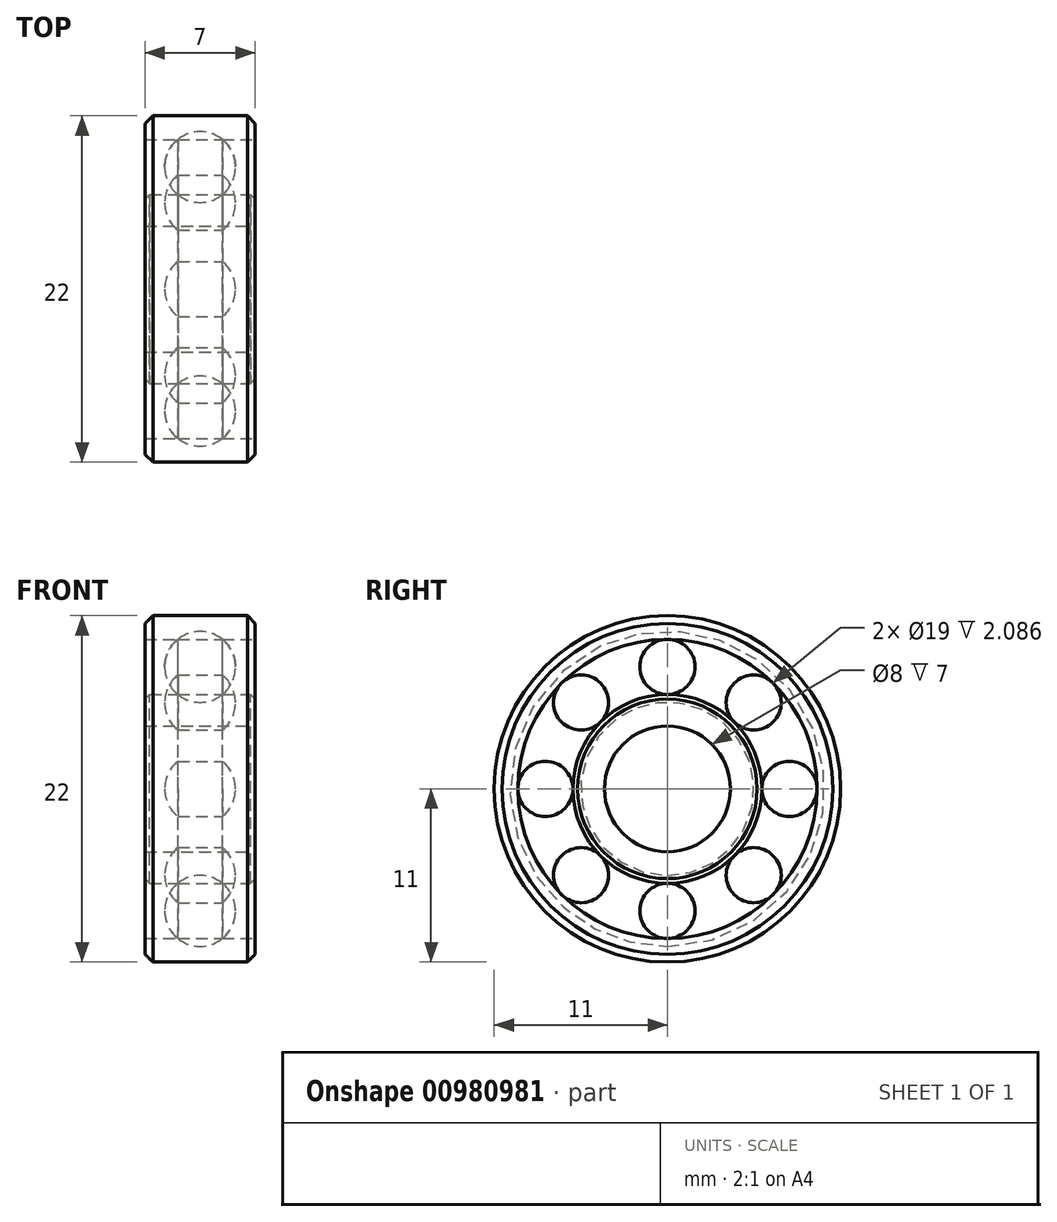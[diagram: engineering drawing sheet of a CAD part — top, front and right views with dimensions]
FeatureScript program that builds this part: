
annotation { "Feature Type Name" : "Feature", "Feature Type Description" : "" }
export const myFeature = defineFeature(function(context is Context, id is Id, definition is map)
    precondition{}
    {
        {
            var Q0;
            Q0=qCreatedBy(makeId("Right.planeOp"),FACE);
            var sketch = newSketch(context, id + "F0", { "sketchPlane" : qUnion([Q0])});
            skLineSegment(sketch, "E0", {"start": v(-11.44, 0) * mm, "end": v(12.35, 0) * mm, "construction": true});
            skCircle(sketch, "E1", {"center": v(0, 7.75) * mm, "radius": 2.25 * mm});
            skLineSegment(sketch, "E2.bottom", {"start": v(-3.5, 4) * mm, "end": v(3.5, 4) * mm});
            skLineSegment(sketch, "E2.top", {"start": v(-3.5, 6) * mm, "end": v(3.5, 6) * mm});
            skLineSegment(sketch, "E2.left", {"start": v(-3.5, 4) * mm, "end": v(-3.5, 6) * mm});
            skLineSegment(sketch, "E2.right", {"start": v(3.5, 4) * mm, "end": v(3.5, 6) * mm});
            skLineSegment(sketch, "E3.bottom", {"start": v(-3.5, 9.5) * mm, "end": v(3.5, 9.5) * mm});
            skLineSegment(sketch, "E3.top", {"start": v(-3.5, 11) * mm, "end": v(3.5, 11) * mm});
            skLineSegment(sketch, "E3.left", {"start": v(-3.5, 9.5) * mm, "end": v(-3.5, 11) * mm});
            skLineSegment(sketch, "E3.right", {"start": v(3.5, 9.5) * mm, "end": v(3.5, 11) * mm});
            skLineSegment(sketch, "E4", {"start": v(0, 0) * mm, "end": v(0, 30.94) * mm, "construction": true});
            skPoint(sketch, "E5", {"position": v(0, 6) * mm});
            skLineSegment(sketch, "E6", {"start": v(-6.72, 7.75) * mm, "end": v(10, 7.75) * mm, "construction": true});
            skLineSegment(sketch, "E7", {"start": v(-2.25, 7.75) * mm, "end": v(2.25, 7.75) * mm});
            skSolve(sketch);
        }
        {
            var Q0;
            Q0=makeQuery(id+"F0.imprint","IMPRINT",FACE,{"disambiguationData":[TD([[makeQuery(id+"F0.imprint","IMPRINT",EDGE,{"derivedFrom":sQuery(id+"F0.wireOp",EDGE,"E2.bottom")}),1.0]])]});
            var Q1;
            Q1=makeQuery(id+"F0.imprint","IMPRINT",FACE,{"disambiguationData":[TD([[makeQuery(id+"F0.imprint","IMPRINT",EDGE,{"derivedFrom":sQuery(id+"F0.wireOp",EDGE,"E3.top")}),-1.0]])]});
            var Q2;
            Q2=sQuery(id+"F0.wireOp",EDGE,"E0");
            revolve(context, id + "F1", {"surfaceOperationType" : NewSurfaceOperationType.NEW, "entities" : qUnion([Q0, Q1]), "axis" : qUnion([Q2]), "revolveType" : RevolveType.FULL});
        }
        {
            var Q0;
            {var subQ0=sQuery(id+"F0.wireOp",EDGE,"E7");Q0=makeQuery(id+"F0.imprint","IMPRINT",FACE,{"disambiguationData":[TD([[makeQuery(id+"F0.imprint","IMPRINT",EDGE,{"derivedFrom":subQ0}),1.0]])]});}
            var Q1;
            {var subQ0=sQuery(id+"F0.wireOp",EDGE,"E3.bottom");var subQ1=sQuery(id+"F0.wireOp",EDGE,"E1");var subQ2=makeQuery(id+"F0.imprint","INTERSECT",VERTEX,{"disambiguationData":[OD(0.0)],"derivedFrom":[subQ1,subQ0]});Q1=makeQuery(id+"F0.imprint","IMPRINT",FACE,{"disambiguationData":[TD([[makeQuery(id+"F0.imprint","IMPRINT",EDGE,{"disambiguationData":[TD([[subQ2,-1.0]])],"derivedFrom":subQ1}),1.0]])]});}
            var Q2;
            Q2=sQuery(id+"F0.wireOp",EDGE,"E6");
            revolve(context, id + "F2", {"surfaceOperationType" : NewSurfaceOperationType.NEW, "entities" : qUnion([Q0, Q1]), "axis" : qUnion([Q2]), "revolveType" : RevolveType.FULL});
        }
        {
            var Q0;
            Q0=makeQuery(id+"F2.opRevolve","SWEPT_BODY",BODY,{"disambiguationData":[OSD([sQuery(id+"F0.wireOp",EDGE,"E1"),sQuery(id+"F0.wireOp",EDGE,"E7")])]});
            var Q1;
            Q1=sQuery(id+"F0.wireOp",EDGE,"E0");
            circularPattern(context, id + "F3", {"entities" : qUnion([Q0]), "axis" : qUnion([Q1]), "angle" : 360 * degree, "instanceCount" : 8, "equalSpace" : true});
        }
        {
            var Q0;
            Q0=makeQuery(id+"F1.opRevolve","SWEPT_EDGE",EDGE,{"disambiguationData":[OSD([sQuery(id+"F0.wireOp",EDGE,"E3.top"),sQuery(id+"F0.wireOp",EDGE,"E3.left")])]});
            var Q1;
            Q1=makeQuery(id+"F1.opRevolve","SWEPT_EDGE",EDGE,{"disambiguationData":[OSD([sQuery(id+"F0.wireOp",EDGE,"E3.top"),sQuery(id+"F0.wireOp",EDGE,"E3.right")])]});
            chamfer(context, id + "F4", {"entities" : qUnion([Q0, Q1]), "width" : 0.5 * mm, "tangentPropagation" : true});
        }
        {
            var Q0;
            Q0=makeQuery(id+"F1.opRevolve","SWEPT_EDGE",EDGE,{"disambiguationData":[OSD([sQuery(id+"F0.wireOp",EDGE,"E2.top"),sQuery(id+"F0.wireOp",EDGE,"E2.left")])]});
            var Q1;
            Q1=makeQuery(id+"F1.opRevolve","SWEPT_EDGE",EDGE,{"disambiguationData":[OSD([sQuery(id+"F0.wireOp",EDGE,"E2.top"),sQuery(id+"F0.wireOp",EDGE,"E2.right")])]});
            chamfer(context, id + "F5", {"entities" : qUnion([Q0, Q1]), "width" : 0.3 * mm, "tangentPropagation" : true});
        }
        {
            var Q0;
            Q0=makeQuery(id+"F3.opPattern","COPY",BODY,{"derivedFrom":makeQuery(id+"F2.opRevolve","SWEPT_BODY",BODY,{"disambiguationData":[OSD([sQuery(id+"F0.wireOp",EDGE,"E1"),sQuery(id+"F0.wireOp",EDGE,"E7")])]}),"instanceName":"3"});
            var Q1;
            Q1=makeQuery(id+"F1.opRevolve","SWEPT_BODY",BODY,{"disambiguationData":[OSD([sQuery(id+"F0.wireOp",EDGE,"E1"),sQuery(id+"F0.wireOp",EDGE,"E2.bottom"),sQuery(id+"F0.wireOp",EDGE,"E2.top"),sQuery(id+"F0.wireOp",EDGE,"E2.left"),sQuery(id+"F0.wireOp",EDGE,"E2.right")])]});
            var Q2;
            Q2=makeQuery(id+"F1.opRevolve","SWEPT_BODY",BODY,{"disambiguationData":[OSD([sQuery(id+"F0.wireOp",EDGE,"E1"),sQuery(id+"F0.wireOp",EDGE,"E3.bottom"),sQuery(id+"F0.wireOp",EDGE,"E3.top"),sQuery(id+"F0.wireOp",EDGE,"E3.left"),sQuery(id+"F0.wireOp",EDGE,"E3.right")])]});
            var Q3;
            Q3=makeQuery(id+"F3.opPattern","COPY",BODY,{"derivedFrom":makeQuery(id+"F2.opRevolve","SWEPT_BODY",BODY,{"disambiguationData":[OSD([sQuery(id+"F0.wireOp",EDGE,"E1"),sQuery(id+"F0.wireOp",EDGE,"E7")])]}),"instanceName":"5"});
            var Q4;
            Q4=makeQuery(id+"F3.opPattern","COPY",BODY,{"derivedFrom":makeQuery(id+"F2.opRevolve","SWEPT_BODY",BODY,{"disambiguationData":[OSD([sQuery(id+"F0.wireOp",EDGE,"E1"),sQuery(id+"F0.wireOp",EDGE,"E7")])]}),"instanceName":"2"});
            var Q5;
            Q5=makeQuery(id+"F3.opPattern","COPY",BODY,{"derivedFrom":makeQuery(id+"F2.opRevolve","SWEPT_BODY",BODY,{"disambiguationData":[OSD([sQuery(id+"F0.wireOp",EDGE,"E1"),sQuery(id+"F0.wireOp",EDGE,"E7")])]}),"instanceName":"4"});
            var Q6;
            Q6=makeQuery(id+"F3.opPattern","COPY",BODY,{"derivedFrom":makeQuery(id+"F2.opRevolve","SWEPT_BODY",BODY,{"disambiguationData":[OSD([sQuery(id+"F0.wireOp",EDGE,"E1"),sQuery(id+"F0.wireOp",EDGE,"E7")])]}),"instanceName":"6"});
            var Q7;
            Q7=makeQuery(id+"F3.opPattern","COPY",BODY,{"derivedFrom":makeQuery(id+"F2.opRevolve","SWEPT_BODY",BODY,{"disambiguationData":[OSD([sQuery(id+"F0.wireOp",EDGE,"E1"),sQuery(id+"F0.wireOp",EDGE,"E7")])]}),"instanceName":"1"});
            var Q8;
            Q8=makeQuery(id+"F3.opPattern","COPY",BODY,{"derivedFrom":makeQuery(id+"F2.opRevolve","SWEPT_BODY",BODY,{"disambiguationData":[OSD([sQuery(id+"F0.wireOp",EDGE,"E1"),sQuery(id+"F0.wireOp",EDGE,"E7")])]}),"instanceName":"7"});
            var Q9;
            Q9=makeQuery(id+"F2.opRevolve","SWEPT_BODY",BODY,{"disambiguationData":[OSD([sQuery(id+"F0.wireOp",EDGE,"E1"),sQuery(id+"F0.wireOp",EDGE,"E7")])]});
            var Q10;
            Q10=sQuery(id+"F0.wireOp",EDGE,"E4");
            transform(context, id + "F6", {"entities" : qUnion([Q0, Q1, Q2, Q3, Q4, Q5, Q6, Q7, Q8, Q9]), "transformType" : TransformType.ROTATION, "transformAxis" : qUnion([Q10]), "angle" : 90 * degree, "makeCopy" : false});
        }
    });
